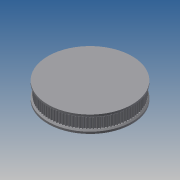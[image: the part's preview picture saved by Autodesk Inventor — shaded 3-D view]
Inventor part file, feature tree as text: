
AUTODESK INVENTOR PART (.ipt)
format: ipt  version: 2013 (Build 170138000, 138)  size: 503,296 bytes
history: native  units: mm
features: extrude x3, sketch x2, pattern_circular x1, chamfer x1, mirror x1
ambient origin geometry x8: Origin, YZ Plane, XZ Plane, XY Plane, X Axis, Y Axis, Z Axis, Center Point
bodies: Solid1 (feature_tree), Solid2 (feature_tree)
feature tree (8):
  extrude  "Extrusion14"  TaperAngle=360.0deg  [1 undecoded]
  extrude  "Extrusion15"  Depth=2.5mm TaperAngle=0.0deg
  pattern_circular  "Circular Pattern1"  Angle=45.0deg  [1 undecoded]
  extrude  "Extrusion3"  Depth=63.153977mm
  chamfer  "Chamfer2"  Distance=8.0mm
  mirror  "Mirror1"
  sketch  "Sketch17"  dims[d11=0.254mm d20=1000.0mm d21=360.0deg]
  sketch  "Sketch18"  dims[d31=1.0mm d32=2.5mm d33=0.0mm d34=1.0mm d35=2.0mm d36=45.0deg d107=63.153977mm d110=8.0mm d111=0.0mm d112=1.59mm d114=8.0mm d115=0.0mm d116=1.0mm]
note: 2 required parameter values undecoded (feature->parameter linkage not recoverable at this tier; creation-order binding heuristic only, values carry confidence <= 0.55)
